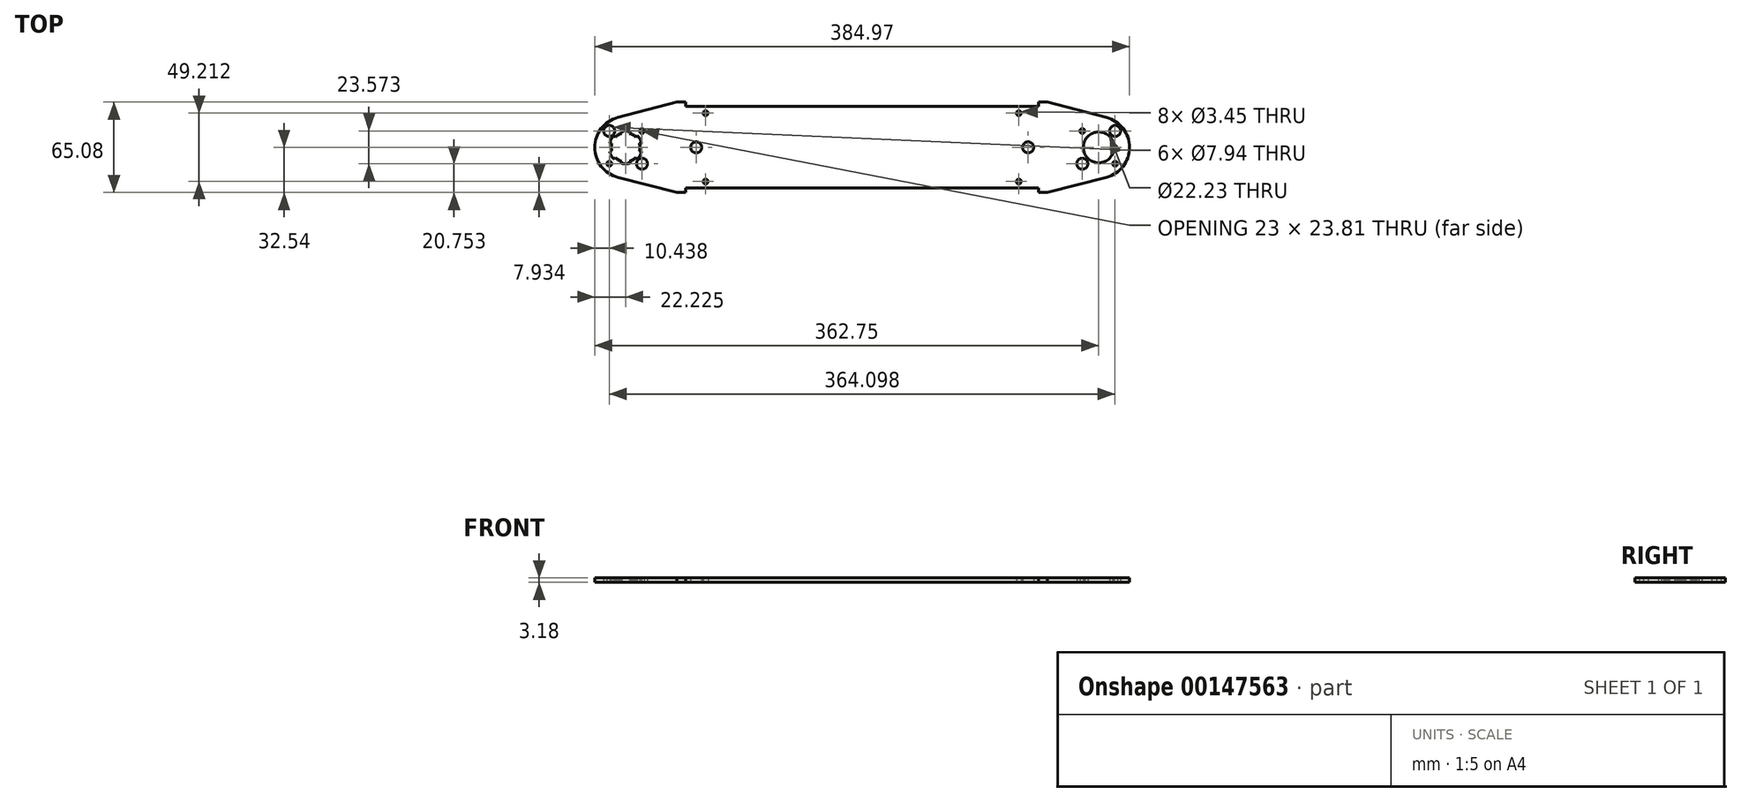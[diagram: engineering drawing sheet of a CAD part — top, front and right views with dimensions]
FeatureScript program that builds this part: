
annotation { "Feature Type Name" : "Feature", "Feature Type Description" : "" }
export const myFeature = defineFeature(function(context is Context, id is Id, definition is map)
    precondition{}
    {
        {
            var Q0;
            Q0=qCreatedBy(makeId("Top.planeOp"),FACE);
            var sketch = newSketch(context, id + "F0", { "sketchPlane" : qUnion([Q0])});
            skPoint(sketch, "E0.rect.middle", {"position": v(0, 0) * mm});
            skCircle(sketch, "E1", {"center": v(0, 0) * mm, "radius": 11.11 * mm});
            skLineSegment(sketch, "E2.bottom", {"start": v(11.79, 11.79) * mm, "end": v(-11.79, 11.79) * mm, "construction": true});
            skLineSegment(sketch, "E2.left", {"start": v(11.79, 11.79) * mm, "end": v(11.79, -11.79) * mm, "construction": true});
            skLineSegment(sketch, "E2.right", {"start": v(-11.79, 11.79) * mm, "end": v(-11.79, -11.79) * mm, "construction": true});
            skCircle(sketch, "E3", {"center": v(11.79, 11.79) * mm, "radius": 5.56 * mm, "construction": true});
            skCircle(sketch, "E4", {"center": v(-11.79, 11.79) * mm, "radius": 1.73 * mm});
            skCircle(sketch, "E5", {"center": v(11.79, 11.79) * mm, "radius": 3.97 * mm});
            skCircle(sketch, "E6", {"center": v(11.79, -11.79) * mm, "radius": 1.73 * mm});
            skCircle(sketch, "E7", {"center": v(-11.79, -11.79) * mm, "radius": 3.97 * mm});
            skArc(sketch, "E8", {"start": v(-346.1, 21.51) * mm, "mid": v(-362.75, 0) * mm, "end": v(-346.1, -21.51) * mm});
            skLineSegment(sketch, "E9.bottom", {"start": v(-352.31, 11.79) * mm, "end": v(-328.74, 11.79) * mm, "construction": true});
            skLineSegment(sketch, "E9.top", {"start": v(-352.31, -11.79) * mm, "end": v(-328.74, -11.79) * mm, "construction": true});
            skLineSegment(sketch, "E9.left", {"start": v(-352.31, 11.79) * mm, "end": v(-352.31, -11.79) * mm, "construction": true});
            skLineSegment(sketch, "E9.right", {"start": v(-328.74, 11.79) * mm, "end": v(-328.74, -11.79) * mm, "construction": true});
            skCircle(sketch, "E10", {"center": v(-328.74, 11.79) * mm, "radius": 1.73 * mm});
            skCircle(sketch, "E11", {"center": v(-340.53, 0) * mm, "radius": 10.32 * mm});
            skCircle(sketch, "E12", {"center": v(-352.31, 11.79) * mm, "radius": 3.97 * mm});
            skCircle(sketch, "E13", {"center": v(-352.31, -11.79) * mm, "radius": 1.73 * mm});
            skCircle(sketch, "E14", {"center": v(-328.74, -11.79) * mm, "radius": 3.97 * mm});
            skLineSegment(sketch, "E15", {"start": v(0, 0) * mm, "end": v(-340.53, 0) * mm, "construction": true});
            skLineSegment(sketch, "E16", {"start": v(-346.1, -21.51) * mm, "end": v(-303.61, -32.54) * mm});
            skLineSegment(sketch, "E17", {"start": v(-346.1, 21.51) * mm, "end": v(-303.61, 32.54) * mm});
            skLineSegment(sketch, "E18", {"start": v(-297.26, -29.37) * mm, "end": v(-43.26, -29.37) * mm});
            skLineSegment(sketch, "E19", {"start": v(-297.26, 29.37) * mm, "end": v(-43.26, 29.37) * mm});
            skLineSegment(sketch, "E20", {"start": v(-297.26, 32.54) * mm, "end": v(-297.26, 29.37) * mm});
            skLineSegment(sketch, "E21", {"start": v(-297.26, 32.54) * mm, "end": v(-303.61, 32.54) * mm});
            skLineSegment(sketch, "E22", {"start": v(-297.26, -29.37) * mm, "end": v(-297.26, -32.54) * mm});
            skLineSegment(sketch, "E23", {"start": v(-297.26, -32.54) * mm, "end": v(-303.61, -32.54) * mm});
            skLineSegment(sketch, "E24", {"start": v(-43.26, -29.37) * mm, "end": v(-43.26, -32.54) * mm});
            skLineSegment(sketch, "E25", {"start": v(-43.26, -32.54) * mm, "end": v(-36.91, -32.54) * mm});
            skLineSegment(sketch, "E26", {"start": v(-43.26, 29.37) * mm, "end": v(-43.26, 32.54) * mm});
            skLineSegment(sketch, "E27", {"start": v(-43.26, 32.54) * mm, "end": v(-36.91, 32.54) * mm});
            skLineSegment(sketch, "E28", {"start": v(-36.91, -32.54) * mm, "end": v(5.58, -21.51) * mm});
            skLineSegment(sketch, "E29", {"start": v(5.58, 21.51) * mm, "end": v(-36.91, 32.54) * mm});
            skArc(sketch, "E30", {"start": v(5.58, -21.51) * mm, "mid": v(22.23, 0) * mm, "end": v(5.58, 21.51) * mm});
            skLineSegment(sketch, "E31", {"start": v(-297.26, 29.37) * mm, "end": v(-297.26, 24.6) * mm, "construction": true});
            skLineSegment(sketch, "E32", {"start": v(-297.26, 24.6) * mm, "end": v(-282.98, 24.6) * mm, "construction": true});
            skLineSegment(sketch, "E33", {"start": v(-297.26, -29.37) * mm, "end": v(-297.26, -24.6) * mm, "construction": true});
            skLineSegment(sketch, "E34", {"start": v(-297.26, -24.6) * mm, "end": v(-282.98, -24.6) * mm, "construction": true});
            skLineSegment(sketch, "E35", {"start": v(-43.26, -29.37) * mm, "end": v(-43.26, -24.6) * mm, "construction": true});
            skLineSegment(sketch, "E36", {"start": v(-43.26, -24.6) * mm, "end": v(-57.55, -24.6) * mm, "construction": true});
            skLineSegment(sketch, "E37", {"start": v(-43.26, 29.37) * mm, "end": v(-43.26, 24.6) * mm, "construction": true});
            skLineSegment(sketch, "E38", {"start": v(-43.26, 24.6) * mm, "end": v(-57.55, 24.6) * mm, "construction": true});
            skCircle(sketch, "E39", {"center": v(-282.98, 24.6) * mm, "radius": 1.73 * mm});
            skCircle(sketch, "E40", {"center": v(-57.55, 24.6) * mm, "radius": 1.73 * mm});
            skCircle(sketch, "E41", {"center": v(-57.55, -24.6) * mm, "radius": 1.73 * mm});
            skCircle(sketch, "E42", {"center": v(-282.98, -24.6) * mm, "radius": 1.73 * mm});
            skLineSegment(sketch, "E43", {"start": v(-11.79, -11.79) * mm, "end": v(11.79, -11.79) * mm, "construction": true});
            skLineSegment(sketch, "E44", {"start": v(-170.26, -29.37) * mm, "end": v(-170.26, 0) * mm, "construction": true});
            skLineSegment(sketch, "E45", {"start": v(-170.26, 0) * mm, "end": v(-170.26, 29.37) * mm, "construction": true});
            skLineSegment(sketch, "E46", {"start": v(-328.74, 11.79) * mm, "end": v(-289.73, 11.79) * mm, "construction": true});
            skLineSegment(sketch, "E47", {"start": v(-289.73, 11.79) * mm, "end": v(-289.73, 0) * mm, "construction": true});
            skLineSegment(sketch, "E48", {"start": v(-11.79, 11.79) * mm, "end": v(-50.8, 11.79) * mm, "construction": true});
            skLineSegment(sketch, "E49", {"start": v(-50.8, 11.79) * mm, "end": v(-50.8, 0) * mm, "construction": true});
            skCircle(sketch, "E50", {"center": v(-50.8, 0) * mm, "radius": 3.97 * mm});
            skCircle(sketch, "E51", {"center": v(-289.73, 0) * mm, "radius": 3.97 * mm});
            skSolve(sketch);
        }
        {
            var Q0;
            Q0=qSketchRegion(id+"F0",true);
            extrude(context, id + "F1", {"entities" : qUnion([Q0]), "depth" : 3.17 * mm});
        }
        {
            var Q0;
            Q0=makeQuery(id+"F1.opExtrude","CAP_FACE",FACE,{"disambiguationData":[OSD([sQuery(id+"F0.wireOp",EDGE,"d63eafa0-1946-4b0e-8293-95e246b273c5.rect.bottom"),sQuery(id+"F0.wireOp",EDGE,"d63eafa0-1946-4b0e-8293-95e246b273c5.rect.top"),sQuery(id+"F0.wireOp",EDGE,"5983dcdd-59a7-4b72-80fd-e4567be1ae8a"),sQuery(id+"F0.wireOp",EDGE,"5a538b3e-fc2b-4d64-affd-5d60433388e5"),sQuery(id+"F0.wireOp",EDGE,"72e86de7-b207-474f-aadf-64543fae3f9b"),sQuery(id+"F0.wireOp",EDGE,"1c038800-5bd5-4753-8b38-6da13ef78ef9"),sQuery(id+"F0.wireOp",EDGE,"EbMUZoU6-Ffds-1dNq-SxhE-hPi8oSjhvaod"),sQuery(id+"F0.wireOp",EDGE,"RfgQjzcw-1Izs-lnTa-bWkk-oBHRDQjbZqQC"),sQuery(id+"F0.wireOp",EDGE,"1cCQAcjj-TyQA-3DMx-kDix-v5yZVaaGeXVM"),sQuery(id+"F0.wireOp",EDGE,"7KPu8lni-3ZWA-t6oJ-FRoh-C5MB3aVr7E9B"),sQuery(id+"F0.wireOp",EDGE,"bSzr06ES-7M0i-Fw5H-UJmt-4e4EQGRPIe4n"),sQuery(id+"F0.wireOp",EDGE,"WGsr6OjU-OX8l-mawA-7cCc-MfOuMOY06Cp5"),sQuery(id+"F0.wireOp",EDGE,"9mrz1cDN-18gM-20ra-6VCO-jp25g10tvNn2"),sQuery(id+"F0.wireOp",EDGE,"G0uOisy3-Mq6h-PcKh-Zkf4-CVoCvP3Hii1l"),sQuery(id+"F0.wireOp",EDGE,"1ae556be-0ab9-4322-b48e-98cf5a741ae0"),sQuery(id+"F0.wireOp",EDGE,"676cd913-43f8-42b3-8cdc-a90136d19ef5"),sQuery(id+"F0.wireOp",EDGE,"xnt2EyF8-ZVyQ-RbWD-GIsP-ThkcyX8ZioIH.bottom"),sQuery(id+"F0.wireOp",EDGE,"xnt2EyF8-ZVyQ-RbWD-GIsP-ThkcyX8ZioIH.top"),sQuery(id+"F0.wireOp",EDGE,"xnt2EyF8-ZVyQ-RbWD-GIsP-ThkcyX8ZioIH.left"),sQuery(id+"F0.wireOp",EDGE,"E1"),sQuery(id+"F0.wireOp",EDGE,"Jo9pZc7T-t0kF-vjz1-dNbX-L65bwNqtrrdz"),sQuery(id+"F0.wireOp",EDGE,"lEYoY9t7-PMOS-SVp6-xfnB-Xp9WdWMCDdum"),sQuery(id+"F0.wireOp",EDGE,"s7aM02SC-9XQ7-dueL-DqMg-ZFuJqOofj9mt"),sQuery(id+"F0.wireOp",EDGE,"deKa9ngt-XMq2-GGkr-SZIa-KlyN0U5bcCDe"),sQuery(id+"F0.wireOp",EDGE,"E4"),sQuery(id+"F0.wireOp",EDGE,"E5"),sQuery(id+"F0.wireOp",EDGE,"E6"),sQuery(id+"F0.wireOp",EDGE,"E7"),sQuery(id+"F0.wireOp",EDGE,"E8"),sQuery(id+"F0.wireOp",EDGE,"E10"),sQuery(id+"F0.wireOp",EDGE,"E11"),sQuery(id+"F0.wireOp",EDGE,"E12"),sQuery(id+"F0.wireOp",EDGE,"E13"),sQuery(id+"F0.wireOp",EDGE,"E14")])],"isStart":true});
            var sketch = newSketch(context, id + "F2", { "sketchPlane" : qUnion([Q0])});
            skLineSegment(sketch, "E52", {"start": v(-340.53, 0) * mm, "end": v(-349.46, -5.16) * mm, "construction": true});
            skArc(sketch, "E53", {"start": v(-350.5, -2.67) * mm, "mid": v(-349.46, -5.16) * mm, "end": v(-347.82, -7.3) * mm});
            skLineSegment(sketch, "E54", {"start": v(-340.53, 0) * mm, "end": v(-347.82, -7.3) * mm, "construction": true});
            skLineSegment(sketch, "E55", {"start": v(-340.53, 0) * mm, "end": v(-350.5, -2.67) * mm, "construction": true});
            skLineSegment(sketch, "E56", {"start": v(-347.82, -7.3) * mm, "end": v(-348.94, -8.42) * mm});
            skLineSegment(sketch, "E57", {"start": v(-350.5, -2.67) * mm, "end": v(-352.03, -3.08) * mm});
            skArc(sketch, "E58", {"start": v(-352.03, -3.08) * mm, "mid": v(-350.84, -5.95) * mm, "end": v(-348.94, -8.42) * mm});
            skLineSegment(sketch, "E59", {"start": v(-340.53, 0) * mm, "end": v(-350.84, 0) * mm, "construction": true});
            skSolve(sketch);
        }
        {
            var Q0;
            Q0=qSketchRegion(id+"F2",true);
            var Q1;
            Q1=makeQuery(id+"F1.opExtrude","CAP_FACE",FACE,{"disambiguationData":[OSD([sQuery(id+"F0.wireOp",EDGE,"d63eafa0-1946-4b0e-8293-95e246b273c5.rect.bottom"),sQuery(id+"F0.wireOp",EDGE,"d63eafa0-1946-4b0e-8293-95e246b273c5.rect.top"),sQuery(id+"F0.wireOp",EDGE,"5983dcdd-59a7-4b72-80fd-e4567be1ae8a"),sQuery(id+"F0.wireOp",EDGE,"5a538b3e-fc2b-4d64-affd-5d60433388e5"),sQuery(id+"F0.wireOp",EDGE,"72e86de7-b207-474f-aadf-64543fae3f9b"),sQuery(id+"F0.wireOp",EDGE,"1c038800-5bd5-4753-8b38-6da13ef78ef9"),sQuery(id+"F0.wireOp",EDGE,"EbMUZoU6-Ffds-1dNq-SxhE-hPi8oSjhvaod"),sQuery(id+"F0.wireOp",EDGE,"RfgQjzcw-1Izs-lnTa-bWkk-oBHRDQjbZqQC"),sQuery(id+"F0.wireOp",EDGE,"1cCQAcjj-TyQA-3DMx-kDix-v5yZVaaGeXVM"),sQuery(id+"F0.wireOp",EDGE,"7KPu8lni-3ZWA-t6oJ-FRoh-C5MB3aVr7E9B"),sQuery(id+"F0.wireOp",EDGE,"bSzr06ES-7M0i-Fw5H-UJmt-4e4EQGRPIe4n"),sQuery(id+"F0.wireOp",EDGE,"WGsr6OjU-OX8l-mawA-7cCc-MfOuMOY06Cp5"),sQuery(id+"F0.wireOp",EDGE,"9mrz1cDN-18gM-20ra-6VCO-jp25g10tvNn2"),sQuery(id+"F0.wireOp",EDGE,"G0uOisy3-Mq6h-PcKh-Zkf4-CVoCvP3Hii1l"),sQuery(id+"F0.wireOp",EDGE,"1ae556be-0ab9-4322-b48e-98cf5a741ae0"),sQuery(id+"F0.wireOp",EDGE,"676cd913-43f8-42b3-8cdc-a90136d19ef5"),sQuery(id+"F0.wireOp",EDGE,"xnt2EyF8-ZVyQ-RbWD-GIsP-ThkcyX8ZioIH.bottom"),sQuery(id+"F0.wireOp",EDGE,"xnt2EyF8-ZVyQ-RbWD-GIsP-ThkcyX8ZioIH.top"),sQuery(id+"F0.wireOp",EDGE,"xnt2EyF8-ZVyQ-RbWD-GIsP-ThkcyX8ZioIH.left"),sQuery(id+"F0.wireOp",EDGE,"E1"),sQuery(id+"F0.wireOp",EDGE,"Jo9pZc7T-t0kF-vjz1-dNbX-L65bwNqtrrdz"),sQuery(id+"F0.wireOp",EDGE,"lEYoY9t7-PMOS-SVp6-xfnB-Xp9WdWMCDdum"),sQuery(id+"F0.wireOp",EDGE,"s7aM02SC-9XQ7-dueL-DqMg-ZFuJqOofj9mt"),sQuery(id+"F0.wireOp",EDGE,"deKa9ngt-XMq2-GGkr-SZIa-KlyN0U5bcCDe"),sQuery(id+"F0.wireOp",EDGE,"E4"),sQuery(id+"F0.wireOp",EDGE,"E5"),sQuery(id+"F0.wireOp",EDGE,"E6"),sQuery(id+"F0.wireOp",EDGE,"E7"),sQuery(id+"F0.wireOp",EDGE,"E8"),sQuery(id+"F0.wireOp",EDGE,"E10"),sQuery(id+"F0.wireOp",EDGE,"E11"),sQuery(id+"F0.wireOp",EDGE,"E12"),sQuery(id+"F0.wireOp",EDGE,"E13"),sQuery(id+"F0.wireOp",EDGE,"E14")])],"isStart":false});
            extrude(context, id + "F3", {"entities" : qUnion([Q0]), "operationType" : NewBodyOperationType.REMOVE, "endBound" : BoundingType.UP_TO_SURFACE, "oppositeDirection" : true, "endBoundEntityFace" : qUnion([Q1]), "depth" : 25.4 * mm});
        }
        {
            var Q0;
            Q0=makeQuery(id+"F3.boolean.opBoolean","COPY",FACE,{"derivedFrom":makeQuery(id+"F3.opExtrude","SWEPT_FACE",FACE,{"disambiguationData":[OSD([sQuery(id+"F2.wireOp",EDGE,"E56")])]})});
            var Q1;
            Q1=makeQuery(id+"F3.boolean.opBoolean","COPY",FACE,{"derivedFrom":makeQuery(id+"F3.opExtrude","SWEPT_FACE",FACE,{"disambiguationData":[OSD([sQuery(id+"F2.wireOp",EDGE,"E58")])]})});
            var Q2;
            Q2=makeQuery(id+"F3.boolean.opBoolean","COPY",FACE,{"derivedFrom":makeQuery(id+"F3.opExtrude","SWEPT_FACE",FACE,{"disambiguationData":[OSD([sQuery(id+"F2.wireOp",EDGE,"E57")])]})});
            var Q3;
            Q3=makeQuery(id+"F1.opExtrude","SWEPT_FACE",FACE,{"disambiguationData":[OSD([sQuery(id+"F0.wireOp",EDGE,"E11")])]});
            circularPattern(context, id + "F4", {"patternType" : PatternType.FACE, "faces" : qUnion([Q0, Q1, Q2]), "axis" : qUnion([Q3]), "angle" : 60 * degree, "instanceCount" : 6});
        }
        {
            var Q0;
            Q0=makeQuery(id+"F1.opExtrude","CAP_FACE",FACE,{"disambiguationData":[OSD([sQuery(id+"F0.wireOp",EDGE,"E1"),sQuery(id+"F0.wireOp",EDGE,"E4"),sQuery(id+"F0.wireOp",EDGE,"E5"),sQuery(id+"F0.wireOp",EDGE,"E6"),sQuery(id+"F0.wireOp",EDGE,"E7"),sQuery(id+"F0.wireOp",EDGE,"E8"),sQuery(id+"F0.wireOp",EDGE,"E10"),sQuery(id+"F0.wireOp",EDGE,"E11"),sQuery(id+"F0.wireOp",EDGE,"E12"),sQuery(id+"F0.wireOp",EDGE,"E13"),sQuery(id+"F0.wireOp",EDGE,"E14"),sQuery(id+"F0.wireOp",EDGE,"E16"),sQuery(id+"F0.wireOp",EDGE,"E17"),sQuery(id+"F0.wireOp",EDGE,"E18"),sQuery(id+"F0.wireOp",EDGE,"E19"),sQuery(id+"F0.wireOp",EDGE,"E20"),sQuery(id+"F0.wireOp",EDGE,"E21"),sQuery(id+"F0.wireOp",EDGE,"E22"),sQuery(id+"F0.wireOp",EDGE,"E23"),sQuery(id+"F0.wireOp",EDGE,"E24"),sQuery(id+"F0.wireOp",EDGE,"E25"),sQuery(id+"F0.wireOp",EDGE,"E26"),sQuery(id+"F0.wireOp",EDGE,"E27"),sQuery(id+"F0.wireOp",EDGE,"E28"),sQuery(id+"F0.wireOp",EDGE,"E29"),sQuery(id+"F0.wireOp",EDGE,"E30"),sQuery(id+"F0.wireOp",EDGE,"E39"),sQuery(id+"F0.wireOp",EDGE,"VBQrvAlw-hTen-gxea-5rdB-eWDYfLApStqa"),sQuery(id+"F0.wireOp",EDGE,"yiHS12IZ-p0bI-Rr18-zCOr-yyMLVT9gFuvF"),sQuery(id+"F0.wireOp",EDGE,"E40"),sQuery(id+"F0.wireOp",EDGE,"E41"),sQuery(id+"F0.wireOp",EDGE,"rRnw4OZJ-V4Nv-Zfje-mNyT-Kr12XnqSrFdH"),sQuery(id+"F0.wireOp",EDGE,"E42"),sQuery(id+"F0.wireOp",EDGE,"j80b8Ypo-zIiU-stA5-HOYK-FsRsFb2xIukV"),sQuery(id+"F0.wireOp",EDGE,"E50"),sQuery(id+"F0.wireOp",EDGE,"E51")])],"isStart":true});
            var sketch = newSketch(context, id + "F5", { "sketchPlane" : qUnion([Q0])});
            skCircle(sketch, "E60", {"center": v(-340.53, 0) * mm, "radius": 11.11 * mm});
            skSolve(sketch);
        }
        {
            var Q0;
            Q0=qSketchRegion(id+"F5",true);
            extrude(context, id + "F6", {"entities" : qUnion([Q0]), "operationType" : NewBodyOperationType.REMOVE, "oppositeDirection" : true, "depth" : 1.95 * mm});
        }
    });
